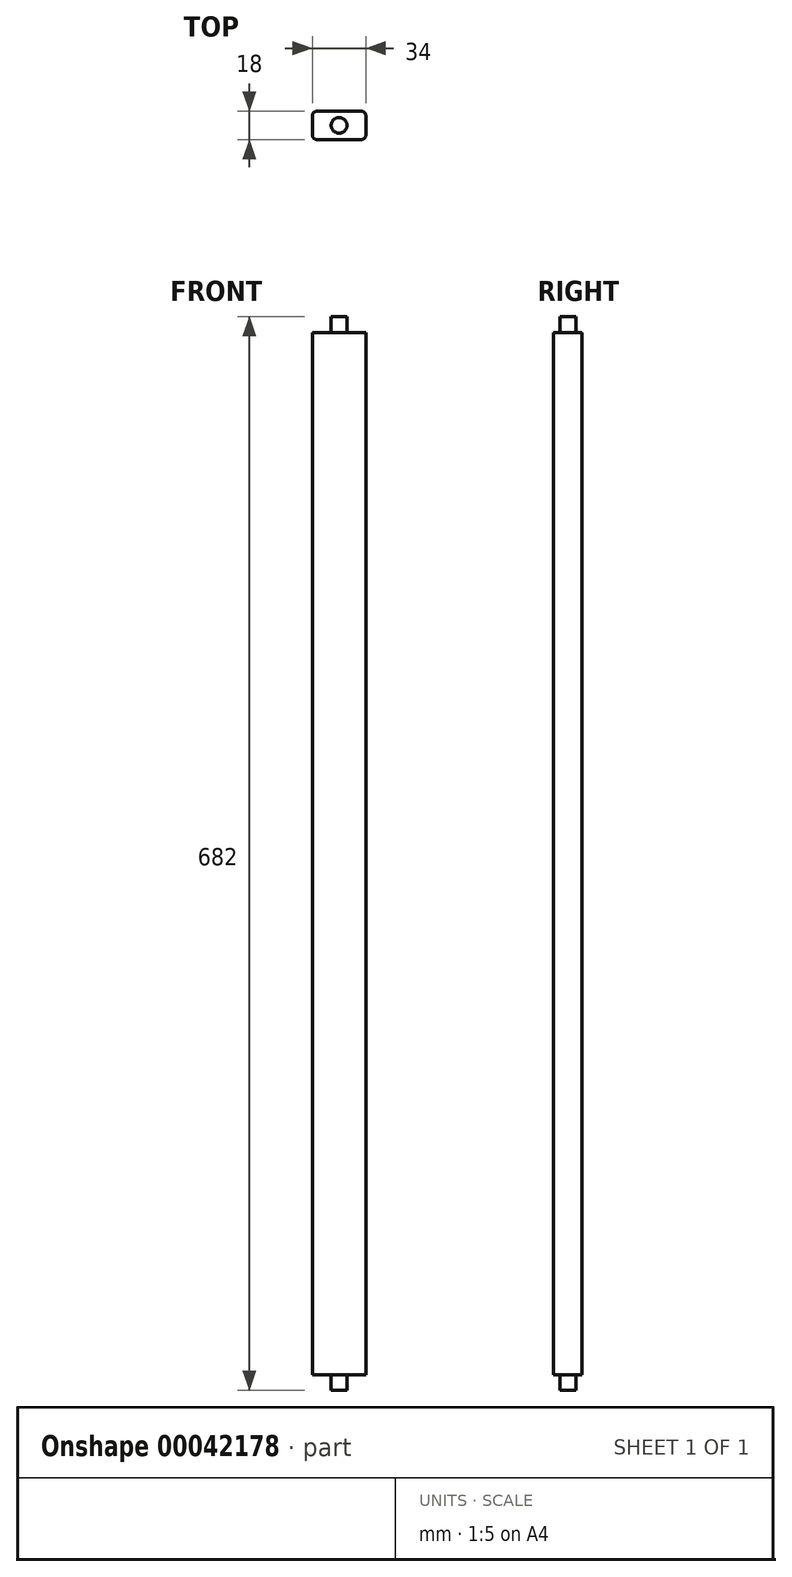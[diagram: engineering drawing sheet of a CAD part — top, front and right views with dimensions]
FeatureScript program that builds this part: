
annotation { "Feature Type Name" : "Feature", "Feature Type Description" : "" }
export const myFeature = defineFeature(function(context is Context, id is Id, definition is map)
    precondition{}
    {
        {
            var Q0;
            Q0=qCreatedBy(makeId("Top.planeOp"),FACE);
            var sketch = newSketch(context, id + "F0", { "sketchPlane" : qUnion([Q0])});
            skLineSegment(sketch, "E0.bottom", {"start": v(0, 0) * mm, "end": v(34, 0) * mm});
            skLineSegment(sketch, "E0.top", {"start": v(0, 18) * mm, "end": v(34, 18) * mm});
            skLineSegment(sketch, "E0.left", {"start": v(0, 0) * mm, "end": v(0, 18) * mm});
            skLineSegment(sketch, "E0.right", {"start": v(34, 0) * mm, "end": v(34, 18) * mm});
            skSolve(sketch);
        }
        {
            var Q0;
            Q0=makeQuery(id+"F0.imprint","IMPRINT",FACE,{"disambiguationData":[TD([[makeQuery(id+"F0.imprint","IMPRINT",EDGE,{"derivedFrom":sQuery(id+"F0.wireOp",EDGE,"E0.bottom")}),1.0]])]});
            extrude(context, id + "F1", {"entities" : qUnion([Q0]), "depth" : 662 * mm});
        }
        {
            var Q0;
            Q0=makeQuery(id+"F1.opExtrude","CAP_FACE",FACE,{"disambiguationData":[OSD([sQuery(id+"F0.wireOp",EDGE,"E0.bottom"),sQuery(id+"F0.wireOp",EDGE,"E0.top"),sQuery(id+"F0.wireOp",EDGE,"E0.left"),sQuery(id+"F0.wireOp",EDGE,"E0.right")])],"isStart":true});
            var sketch = newSketch(context, id + "F2", { "sketchPlane" : qUnion([Q0])});
            skLineSegment(sketch, "E1", {"start": v(17, 0) * mm, "end": v(17, -18) * mm, "construction": true});
            skCircle(sketch, "E2", {"center": v(17, -9) * mm, "radius": 5 * mm});
            skSolve(sketch);
        }
        {
            var Q0;
            Q0=makeQuery(id+"F2.imprint","IMPRINT",FACE,{"disambiguationData":[TD([[makeQuery(id+"F2.imprint","IMPRINT",EDGE,{"derivedFrom":sQuery(id+"F2.wireOp",EDGE,"E2")}),1.0]])]});
            extrude(context, id + "F3", {"entities" : qUnion([Q0]), "operationType" : NewBodyOperationType.ADD, "depth" : 10 * mm, "hasSecondDirection" : true, "secondDirectionOppositeDirection" : true, "secondDirectionDepth" : 672 * mm});
        }
        {
            var Q0;
            Q0=makeQuery(id+"F1.opExtrude","SWEPT_EDGE",EDGE,{"disambiguationData":[OSD([sQuery(id+"F0.wireOp",EDGE,"E0.bottom"),sQuery(id+"F0.wireOp",EDGE,"E0.left")])]});
            var Q1;
            Q1=makeQuery(id+"F1.opExtrude","SWEPT_EDGE",EDGE,{"disambiguationData":[OSD([sQuery(id+"F0.wireOp",EDGE,"E0.top"),sQuery(id+"F0.wireOp",EDGE,"E0.left")])]});
            var Q2;
            Q2=makeQuery(id+"F1.opExtrude","SWEPT_EDGE",EDGE,{"disambiguationData":[OSD([sQuery(id+"F0.wireOp",EDGE,"E0.top"),sQuery(id+"F0.wireOp",EDGE,"E0.right")])]});
            var Q3;
            Q3=makeQuery(id+"F1.opExtrude","SWEPT_EDGE",EDGE,{"disambiguationData":[OSD([sQuery(id+"F0.wireOp",EDGE,"E0.bottom"),sQuery(id+"F0.wireOp",EDGE,"E0.right")])]});
            fillet(context, id + "F4", {"entities" : qUnion([Q0, Q1, Q2, Q3]), "radius" : 3 * mm, "tangentPropagation" : true, "allowEdgeOverflow" : false});
        }
    });
